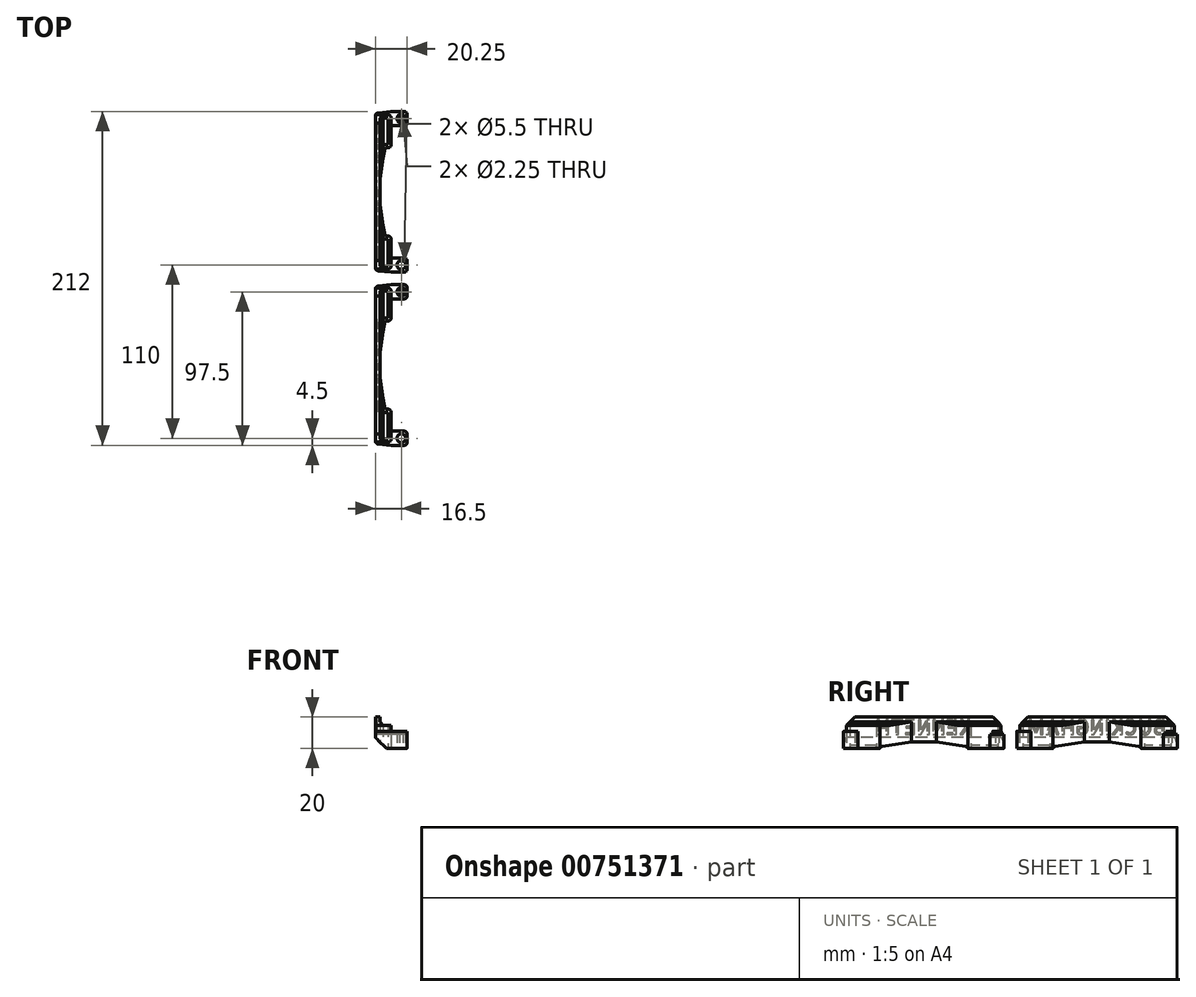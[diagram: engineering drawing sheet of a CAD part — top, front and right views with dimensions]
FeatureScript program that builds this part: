
annotation { "Feature Type Name" : "Feature", "Feature Type Description" : "" }
export const myFeature = defineFeature(function(context is Context, id is Id, definition is map)
    precondition{}
    {
        {
            var Q0;
            Q0=qCreatedBy(makeId("Top.planeOp"),FACE);
            var sketch = newSketch(context, id + "F0", { "sketchPlane" : qUnion([Q0])});
            skLineSegment(sketch, "E0", {"start": v(0, 28) * mm, "end": v(0, -28) * mm, "construction": true});
            skPoint(sketch, "E1", {"position": v(0, 0) * mm});
            skLineSegment(sketch, "E2", {"start": v(0, 28) * mm, "end": v(0, 30) * mm});
            skLineSegment(sketch, "E3", {"start": v(0, 30) * mm, "end": v(0, 47) * mm});
            skLineSegment(sketch, "E4", {"start": v(0, 47) * mm, "end": v(-3, 47) * mm});
            skLineSegment(sketch, "E5", {"start": v(-3, 47) * mm, "end": v(-3, 30) * mm});
            skLineSegment(sketch, "E6", {"start": v(-3, 30) * mm, "end": v(0, 30) * mm});
            skLineSegment(sketch, "E7", {"start": v(-36.95, 0) * mm, "end": v(42, 0) * mm, "construction": true});
            skLineSegment(sketch, "E8", {"start": v(0, 0) * mm, "end": v(8.5, 0) * mm, "construction": true});
            skLineSegment(sketch, "E9", {"start": v(8.5, 46.5) * mm, "end": v(8.5, -46.5) * mm, "construction": true});
            skPoint(sketch, "E10", {"position": v(8.5, 0) * mm});
            skCircle(sketch, "E11", {"center": v(8.5, 46.5) * mm, "radius": 1.13 * mm});
            skCircle(sketch, "E12", {"center": v(8.5, 46.5) * mm, "radius": 2.75 * mm});
            skLineSegment(sketch, "E13.0", {"start": v(2, 28) * mm, "end": v(2, 49) * mm});
            skLineSegment(sketch, "E13.1", {"start": v(-5, 28) * mm, "end": v(2, 28) * mm});
            skLineSegment(sketch, "E13.2", {"start": v(-5, 49) * mm, "end": v(-5, 28) * mm});
            skLineSegment(sketch, "E13.3", {"start": v(2, 49) * mm, "end": v(-5, 49) * mm});
            skLineSegment(sketch, "E14", {"start": v(-5, 49) * mm, "end": v(-8, 49) * mm});
            skLineSegment(sketch, "E15", {"start": v(-8, 49) * mm, "end": v(-8, 50) * mm});
            skLineSegment(sketch, "E16.MirrorCS", {"start": v(-5, -28) * mm, "end": v(2, -28) * mm});
            skLineSegment(sketch, "E17.MirrorCS", {"start": v(2, -28) * mm, "end": v(2, -49) * mm});
            skLineSegment(sketch, "E18.MirrorCS", {"start": v(-5, -49) * mm, "end": v(-5, -28) * mm});
            skLineSegment(sketch, "E19.MirrorCS", {"start": v(2, -49) * mm, "end": v(-5, -49) * mm});
            skLineSegment(sketch, "E20.MirrorCS", {"start": v(0, -30) * mm, "end": v(0, -47) * mm});
            skLineSegment(sketch, "E21.MirrorCS", {"start": v(0, -47) * mm, "end": v(-3, -47) * mm});
            skLineSegment(sketch, "E22.MirrorCS", {"start": v(-3, -47) * mm, "end": v(-3, -30) * mm});
            skLineSegment(sketch, "E23.MirrorCS", {"start": v(-3, -30) * mm, "end": v(0, -30) * mm});
            skLineSegment(sketch, "E24.MirrorCS", {"start": v(-5, -49) * mm, "end": v(-8, -49) * mm});
            skLineSegment(sketch, "E25.MirrorCS", {"start": v(-8, -49) * mm, "end": v(-8, -50) * mm});
            skCircle(sketch, "E26.MirrorC", {"center": v(8.5, -46.5) * mm, "radius": 2.75 * mm});
            skCircle(sketch, "E27.MirrorC", {"center": v(8.5, -46.5) * mm, "radius": 1.13 * mm});
            skLineSegment(sketch, "E28", {"start": v(-8, 49) * mm, "end": v(-8, -49) * mm});
            skLineSegment(sketch, "E29", {"start": v(-5, -28) * mm, "end": v(-5, 28) * mm});
            skLineSegment(sketch, "E30", {"start": v(8.5, 46.5) * mm, "end": v(12.25, 46.5) * mm, "construction": true});
            skLineSegment(sketch, "E31", {"start": v(12.25, 51) * mm, "end": v(12.25, 42) * mm});
            skPoint(sketch, "E32.positionSnap0", {"position": v(12.25, 46.5) * mm});
            skLineSegment(sketch, "E33", {"start": v(12.25, 51) * mm, "end": v(2, 51) * mm});
            skLineSegment(sketch, "E34", {"start": v(2, 51) * mm, "end": v(-8, 50) * mm});
            skLineSegment(sketch, "E35", {"start": v(12.25, 42) * mm, "end": v(2, 42) * mm});
            skLineSegment(sketch, "E36.MirrorCS", {"start": v(12.25, -42) * mm, "end": v(2, -42) * mm});
            skLineSegment(sketch, "E37.MirrorCS", {"start": v(12.25, -51) * mm, "end": v(12.25, -42) * mm});
            skLineSegment(sketch, "E38.MirrorCS", {"start": v(12.25, -51) * mm, "end": v(2, -51) * mm});
            skLineSegment(sketch, "E39.MirrorCS", {"start": v(2, -51) * mm, "end": v(-8, -50) * mm});
            skSolve(sketch);
        }
        {
            var Q0;
            Q0=makeQuery(id+"F0.imprint","IMPRINT",FACE,{"disambiguationData":[TD([[makeQuery(id+"F0.imprint","IMPRINT",EDGE,{"derivedFrom":sQuery(id+"F0.wireOp",EDGE,"E3")}),-1.0]])]});
            var Q1;
            {var subQ3=sQuery(id+"F0.wireOp",EDGE,"E16.MirrorCS");Q1=makeQuery(id+"F0.imprint","IMPRINT",FACE,{"disambiguationData":[TD([[makeQuery(id+"F0.imprint","IMPRINT",EDGE,{"derivedFrom":subQ3}),-1.0]])]});}
            var Q2;
            Q2=makeQuery(id+"F0.imprint","IMPRINT",FACE,{"disambiguationData":[TD([[makeQuery(id+"F0.imprint","IMPRINT",EDGE,{"derivedFrom":sQuery(id+"F0.wireOp",EDGE,"E13.2")}),-1.0]])]});
            extrude(context, id + "F1", {"entities" : qUnion([Q0, Q1, Q2]), "depth" : 14.75 * mm, "offsetDistance" : 25 * mm});
        }
        {
            var Q0;
            {var subQ0=sQuery(id+"F0.wireOp",EDGE,"E19.MirrorCS");Q0=makeQuery(id+"F0.imprint","IMPRINT",FACE,{"disambiguationData":[TD([[makeQuery(id+"F0.imprint","IMPRINT",EDGE,{"derivedFrom":subQ0}),1.0]])]});}
            var Q1;
            Q1=makeQuery(id+"F0.imprint","IMPRINT",FACE,{"disambiguationData":[TD([[makeQuery(id+"F0.imprint","IMPRINT",EDGE,{"derivedFrom":sQuery(id+"F0.wireOp",EDGE,"E12")}),-1.0]])]});
            extrude(context, id + "F2", {"entities" : qUnion([Q0, Q1]), "operationType" : NewBodyOperationType.ADD, "depth" : 9 * mm, "offsetDistance" : 25 * mm});
        }
        {
            var Q0;
            Q0=makeQuery(id+"F0.imprint","IMPRINT",FACE,{"disambiguationData":[TD([[makeQuery(id+"F0.imprint","IMPRINT",EDGE,{"derivedFrom":sQuery(id+"F0.wireOp",EDGE,"E26.MirrorC")}),-1.0]])]});
            var Q1;
            Q1=makeQuery(id+"F0.imprint","IMPRINT",FACE,{"disambiguationData":[TD([[makeQuery(id+"F0.imprint","IMPRINT",EDGE,{"derivedFrom":sQuery(id+"F0.wireOp",EDGE,"E11")}),-1.0]])]});
            extrude(context, id + "F3", {"entities" : qUnion([Q0, Q1]), "operationType" : NewBodyOperationType.ADD, "depth" : 10.9 * mm, "offsetDistance" : 25 * mm});
        }
        {
            var Q0;
            Q0=makeQuery(id+"F0.imprint","IMPRINT",FACE,{"disambiguationData":[TD([[makeQuery(id+"F0.imprint","IMPRINT",EDGE,{"derivedFrom":sQuery(id+"F0.wireOp",EDGE,"E13.2")}),-1.0]])]});
            extrude(context, id + "F4", {"entities" : qUnion([Q0]), "operationType" : NewBodyOperationType.ADD, "depth" : 20 * mm, "offsetDistance" : 25 * mm});
        }
        {
            var Q0;
            Q0=makeQuery(id+"F2.boolean.opBoolean","MERGE",EDGE,{"derivedFrom":[makeQuery(id+"F1.opExtrude","CAP_EDGE",EDGE,{"disambiguationData":[OSD([sQuery(id+"F0.wireOp",EDGE,"E28")])],"isStart":true}),makeQuery(id+"F2.opExtrude","CAP_EDGE",EDGE,{"disambiguationData":[OSD([sQuery(id+"F0.wireOp",EDGE,"E15")])],"isStart":true}),makeQuery(id+"F2.opExtrude","CAP_EDGE",EDGE,{"disambiguationData":[OSD([sQuery(id+"F0.wireOp",EDGE,"E25.MirrorCS")])],"isStart":true})]});
            chamfer(context, id + "F5", {"entities" : qUnion([Q0]), "chamferType" : ChamferType.TWO_OFFSETS, "width1" : 7 * mm, "oppositeDirection" : false, "width2" : 7 * mm, "tangentPropagation" : true});
        }
        {
            var Q0;
            Q0=makeQuery(id+"F1.opExtrude","SWEPT_EDGE",EDGE,{"disambiguationData":[OSD([sQuery(id+"F0.wireOp",EDGE,"E13.1"),sQuery(id+"F0.wireOp",EDGE,"E13.2"),sQuery(id+"F0.wireOp",EDGE,"E29")])]});
            var Q1;
            Q1=makeQuery(id+"F1.opExtrude","SWEPT_EDGE",EDGE,{"disambiguationData":[OSD([sQuery(id+"F0.wireOp",EDGE,"E16.MirrorCS"),sQuery(id+"F0.wireOp",EDGE,"E18.MirrorCS"),sQuery(id+"F0.wireOp",EDGE,"E29")])]});
            chamfer(context, id + "F6", {"entities" : qUnion([Q0, Q1]), "chamferType" : ChamferType.TWO_OFFSETS, "width1" : 3 * mm, "oppositeDirection" : false, "width2" : 20 * mm, "tangentPropagation" : true});
        }
        {
            var Q0;
            Q0=makeQuery(id+"F1.opExtrude","SWEPT_EDGE",EDGE,{"disambiguationData":[OSD([sQuery(id+"F0.wireOp",EDGE,"E13.0"),sQuery(id+"F0.wireOp",EDGE,"E13.1")])]});
            var Q1;
            Q1=makeQuery(id+"F1.opExtrude","SWEPT_EDGE",EDGE,{"disambiguationData":[OSD([sQuery(id+"F0.wireOp",EDGE,"E16.MirrorCS"),sQuery(id+"F0.wireOp",EDGE,"E17.MirrorCS")])]});
            var Q2;
            {var subQ0=sQuery(id+"F0.wireOp",EDGE,"E13.1");Q2=makeQuery(id+"F6.opChamfer","BLEND_EDGE",EDGE,{"blendedFrom":[makeQuery(id+"F1.opExtrude","SWEPT_EDGE",EDGE,{"disambiguationData":[OSD([subQ0,sQuery(id+"F0.wireOp",EDGE,"E13.2"),sQuery(id+"F0.wireOp",EDGE,"E29")])]}),makeQuery(id+"F1.opExtrude","SWEPT_FACE",FACE,{"disambiguationData":[OSD([subQ0])]})],"blendedInto":[makeQuery(id+"F1.opExtrude","SWEPT_FACE",FACE,{"disambiguationData":[OSD([subQ0])]})]});}
            var Q3;
            {var subQ0=sQuery(id+"F0.wireOp",EDGE,"E16.MirrorCS");Q3=makeQuery(id+"F6.opChamfer","BLEND_EDGE",EDGE,{"blendedFrom":[makeQuery(id+"F1.opExtrude","SWEPT_EDGE",EDGE,{"disambiguationData":[OSD([subQ0,sQuery(id+"F0.wireOp",EDGE,"E18.MirrorCS"),sQuery(id+"F0.wireOp",EDGE,"E29")])]}),makeQuery(id+"F1.opExtrude","SWEPT_FACE",FACE,{"disambiguationData":[OSD([subQ0])]})],"blendedInto":[makeQuery(id+"F1.opExtrude","SWEPT_FACE",FACE,{"disambiguationData":[OSD([subQ0])]})]});}
            var Q4;
            Q4=makeQuery(id+"F2.opExtrude","SWEPT_EDGE",EDGE,{"disambiguationData":[OSD([sQuery(id+"F0.wireOp",EDGE,"E25.MirrorCS"),sQuery(id+"F0.wireOp",EDGE,"E39.MirrorCS")])]});
            var Q5;
            Q5=makeQuery(id+"F2.opExtrude","SWEPT_EDGE",EDGE,{"disambiguationData":[OSD([sQuery(id+"F0.wireOp",EDGE,"E38.MirrorCS"),sQuery(id+"F0.wireOp",EDGE,"E39.MirrorCS")])]});
            var Q6;
            Q6=makeQuery(id+"F2.opExtrude","SWEPT_EDGE",EDGE,{"disambiguationData":[OSD([sQuery(id+"F0.wireOp",EDGE,"E15"),sQuery(id+"F0.wireOp",EDGE,"E34")])]});
            var Q7;
            Q7=makeQuery(id+"F2.opExtrude","SWEPT_EDGE",EDGE,{"disambiguationData":[OSD([sQuery(id+"F0.wireOp",EDGE,"E33"),sQuery(id+"F0.wireOp",EDGE,"E34")])]});
            var Q8;
            Q8=makeQuery(id+"F1.opExtrude","SWEPT_EDGE",EDGE,{"disambiguationData":[OSD([sQuery(id+"F0.wireOp",EDGE,"E13.0"),sQuery(id+"F0.wireOp",EDGE,"E13.3")])]});
            var Q9;
            Q9=makeQuery(id+"F1.opExtrude","SWEPT_EDGE",EDGE,{"disambiguationData":[OSD([sQuery(id+"F0.wireOp",EDGE,"E17.MirrorCS"),sQuery(id+"F0.wireOp",EDGE,"E19.MirrorCS")])]});
            var Q10;
            Q10=makeQuery(id+"F2.opExtrude","SWEPT_EDGE",EDGE,{"disambiguationData":[OSD([sQuery(id+"F0.wireOp",EDGE,"E36.MirrorCS"),sQuery(id+"F0.wireOp",EDGE,"E37.MirrorCS")])]});
            var Q11;
            Q11=makeQuery(id+"F2.opExtrude","SWEPT_EDGE",EDGE,{"disambiguationData":[OSD([sQuery(id+"F0.wireOp",EDGE,"E37.MirrorCS"),sQuery(id+"F0.wireOp",EDGE,"E38.MirrorCS")])]});
            var Q12;
            Q12=makeQuery(id+"F2.opExtrude","SWEPT_EDGE",EDGE,{"disambiguationData":[OSD([sQuery(id+"F0.wireOp",EDGE,"E31"),sQuery(id+"F0.wireOp",EDGE,"E35")])]});
            var Q13;
            Q13=makeQuery(id+"F2.opExtrude","SWEPT_EDGE",EDGE,{"disambiguationData":[OSD([sQuery(id+"F0.wireOp",EDGE,"E31"),sQuery(id+"F0.wireOp",EDGE,"E33")])]});
            var Q14;
            Q14=makeQuery(id+"F2.opExtrude","SWEPT_EDGE",EDGE,{"disambiguationData":[OSD([sQuery(id+"F0.wireOp",EDGE,"E13.0"),sQuery(id+"F0.wireOp",EDGE,"E35")])]});
            var Q15;
            Q15=makeQuery(id+"F2.opExtrude","SWEPT_EDGE",EDGE,{"disambiguationData":[OSD([sQuery(id+"F0.wireOp",EDGE,"E17.MirrorCS"),sQuery(id+"F0.wireOp",EDGE,"E36.MirrorCS")])]});
            fillet(context, id + "F7", {"entities" : qUnion([Q0, Q1, Q2, Q3, Q4, Q5, Q6, Q7, Q8, Q9, Q10, Q11, Q12, Q13, Q14, Q15]), "radius" : 2 * mm, "tangentPropagation" : true, "allowEdgeOverflow" : false});
        }
        {
            var Q0;
            {var subQ0=sQuery(id+"F0.wireOp",EDGE,"E29");Q0=makeQuery(id+"F4.boolean.opBoolean","INTERSECT",EDGE,{"disambiguationData":[OD(1.0)],"derivedFrom":[makeQuery(id+"F1.opExtrude","CAP_FACE",FACE,{"disambiguationData":[OSD([sQuery(id+"F0.wireOp",EDGE,"E3"),sQuery(id+"F0.wireOp",EDGE,"E4"),sQuery(id+"F0.wireOp",EDGE,"E5"),sQuery(id+"F0.wireOp",EDGE,"E6"),sQuery(id+"F0.wireOp",EDGE,"E13.0"),sQuery(id+"F0.wireOp",EDGE,"E13.1"),sQuery(id+"F0.wireOp",EDGE,"E13.3"),sQuery(id+"F0.wireOp",EDGE,"E14"),sQuery(id+"F0.wireOp",EDGE,"E16.MirrorCS"),sQuery(id+"F0.wireOp",EDGE,"E17.MirrorCS"),sQuery(id+"F0.wireOp",EDGE,"E19.MirrorCS"),sQuery(id+"F0.wireOp",EDGE,"E20.MirrorCS"),sQuery(id+"F0.wireOp",EDGE,"E21.MirrorCS"),sQuery(id+"F0.wireOp",EDGE,"E22.MirrorCS"),sQuery(id+"F0.wireOp",EDGE,"E23.MirrorCS"),sQuery(id+"F0.wireOp",EDGE,"E24.MirrorCS"),sQuery(id+"F0.wireOp",EDGE,"E28"),subQ0])],"isStart":false}),makeQuery(id+"F4.opExtrude","SWEPT_FACE",FACE,{"disambiguationData":[OSD([sQuery(id+"F0.wireOp",EDGE,"E13.2"),sQuery(id+"F0.wireOp",EDGE,"E18.MirrorCS"),subQ0])]})]});}
            var Q1;
            {var subQ0=sQuery(id+"F0.wireOp",EDGE,"E29");Q1=makeQuery(id+"F4.boolean.opBoolean","INTERSECT",EDGE,{"disambiguationData":[OD(0.0)],"derivedFrom":[makeQuery(id+"F1.opExtrude","CAP_FACE",FACE,{"disambiguationData":[OSD([sQuery(id+"F0.wireOp",EDGE,"E3"),sQuery(id+"F0.wireOp",EDGE,"E4"),sQuery(id+"F0.wireOp",EDGE,"E5"),sQuery(id+"F0.wireOp",EDGE,"E6"),sQuery(id+"F0.wireOp",EDGE,"E13.0"),sQuery(id+"F0.wireOp",EDGE,"E13.1"),sQuery(id+"F0.wireOp",EDGE,"E13.3"),sQuery(id+"F0.wireOp",EDGE,"E14"),sQuery(id+"F0.wireOp",EDGE,"E16.MirrorCS"),sQuery(id+"F0.wireOp",EDGE,"E17.MirrorCS"),sQuery(id+"F0.wireOp",EDGE,"E19.MirrorCS"),sQuery(id+"F0.wireOp",EDGE,"E20.MirrorCS"),sQuery(id+"F0.wireOp",EDGE,"E21.MirrorCS"),sQuery(id+"F0.wireOp",EDGE,"E22.MirrorCS"),sQuery(id+"F0.wireOp",EDGE,"E23.MirrorCS"),sQuery(id+"F0.wireOp",EDGE,"E24.MirrorCS"),sQuery(id+"F0.wireOp",EDGE,"E28"),subQ0])],"isStart":false}),makeQuery(id+"F4.opExtrude","SWEPT_FACE",FACE,{"disambiguationData":[OSD([sQuery(id+"F0.wireOp",EDGE,"E13.2"),sQuery(id+"F0.wireOp",EDGE,"E18.MirrorCS"),subQ0])]})]});}
            chamfer(context, id + "F8", {"entities" : qUnion([Q0, Q1]), "width" : 2 * mm, "tangentPropagation" : true});
        }
        {
            var Q0;
            Q0=makeQuery(id+"F4.opExtrude","CAP_EDGE",EDGE,{"disambiguationData":[OSD([sQuery(id+"F0.wireOp",EDGE,"E24.MirrorCS")])],"isStart":false});
            var Q1;
            Q1=makeQuery(id+"F4.opExtrude","CAP_EDGE",EDGE,{"disambiguationData":[OSD([sQuery(id+"F0.wireOp",EDGE,"E14")])],"isStart":false});
            chamfer(context, id + "F9", {"entities" : qUnion([Q0, Q1]), "width" : 5.25 * mm, "tangentPropagation" : true});
        }
        {
            var Q0;
            Q0=makeQuery(id+"F1.opExtrude","SWEPT_BODY",BODY,{"disambiguationData":[OSD([sQuery(id+"F0.wireOp",EDGE,"E3"),sQuery(id+"F0.wireOp",EDGE,"E4"),sQuery(id+"F0.wireOp",EDGE,"E5"),sQuery(id+"F0.wireOp",EDGE,"E6"),sQuery(id+"F0.wireOp",EDGE,"E13.0"),sQuery(id+"F0.wireOp",EDGE,"E13.1"),sQuery(id+"F0.wireOp",EDGE,"E13.3"),sQuery(id+"F0.wireOp",EDGE,"E14"),sQuery(id+"F0.wireOp",EDGE,"E16.MirrorCS"),sQuery(id+"F0.wireOp",EDGE,"E17.MirrorCS"),sQuery(id+"F0.wireOp",EDGE,"E19.MirrorCS"),sQuery(id+"F0.wireOp",EDGE,"E20.MirrorCS"),sQuery(id+"F0.wireOp",EDGE,"E21.MirrorCS"),sQuery(id+"F0.wireOp",EDGE,"E22.MirrorCS"),sQuery(id+"F0.wireOp",EDGE,"E23.MirrorCS"),sQuery(id+"F0.wireOp",EDGE,"E24.MirrorCS"),sQuery(id+"F0.wireOp",EDGE,"E28"),sQuery(id+"F0.wireOp",EDGE,"E29")])]});
            transform(context, id + "F10", {"entities" : qUnion([Q0]), "transformType" : TransformType.TRANSLATION_3D, "dx" : 0 * mm, "dy" : 110 * mm, "dz" : 0 * mm, "makeCopy" : true});
        }
        {
            var Q0;
            {var subQ0=sQuery(id+"F0.wireOp",EDGE,"E28");Q0=makeQuery(id+"F4.boolean.opBoolean","MERGE",FACE,{"derivedFrom":[makeQuery(id+"F2.boolean.opBoolean","MERGE",FACE,{"derivedFrom":[makeQuery(id+"F1.opExtrude","SWEPT_FACE",FACE,{"disambiguationData":[OSD([subQ0])]}),makeQuery(id+"F2.opExtrude","SWEPT_FACE",FACE,{"disambiguationData":[OSD([sQuery(id+"F0.wireOp",EDGE,"E15")])]}),makeQuery(id+"F2.opExtrude","SWEPT_FACE",FACE,{"disambiguationData":[OSD([sQuery(id+"F0.wireOp",EDGE,"E25.MirrorCS")])]})]}),makeQuery(id+"F4.opExtrude","SWEPT_FACE",FACE,{"disambiguationData":[OSD([subQ0])]})]});}
            var sketch = newSketch(context, id + "F11", { "sketchPlane" : qUnion([Q0])});
            skLineSegment(sketch, "E40", {"start": v(0, 7) * mm, "end": v(0, 20) * mm, "construction": true});
            skPoint(sketch, "E41", {"position": v(0, 13.5) * mm});
            skText(sketch, "E42", { "text": "KENNETH", "fontName": "AllertaStencil-Regular.ttf"});
            skLineSegment(sketch, "E43", {"start": v(-30.55, 14) * mm, "end": v(-30.55, 13) * mm});
            skPoint(sketch, "E44", {"position": v(-30.55, 13.5) * mm});
            skLineSegment(sketch, "E45", {"start": v(-30.55, 14) * mm, "end": v(30.55, 14) * mm, "construction": true});
            skLineSegment(sketch, "E46", {"start": v(-30.55, 13) * mm, "end": v(30.55, 13) * mm, "construction": true});
            skLineSegment(sketch, "E47", {"start": v(30.55, 13) * mm, "end": v(30.55, 14) * mm});
            const initialGuessF11  = {"E42": [-0.03055, 0.00875, 1, 0, 0.0095]};
            skSetInitialGuess(sketch, initialGuessF11);
            skSolve(sketch);
        }
        {
            var Q0;
            {var subQ0=sQuery(id+"F0.wireOp",EDGE,"E28");Q0=makeQuery(id+"F10.opPattern","COPY",FACE,{"derivedFrom":makeQuery(id+"F4.boolean.opBoolean","MERGE",FACE,{"derivedFrom":[makeQuery(id+"F2.boolean.opBoolean","MERGE",FACE,{"derivedFrom":[makeQuery(id+"F1.opExtrude","SWEPT_FACE",FACE,{"disambiguationData":[OSD([subQ0])]}),makeQuery(id+"F2.opExtrude","SWEPT_FACE",FACE,{"disambiguationData":[OSD([sQuery(id+"F0.wireOp",EDGE,"E15")])]}),makeQuery(id+"F2.opExtrude","SWEPT_FACE",FACE,{"disambiguationData":[OSD([sQuery(id+"F0.wireOp",EDGE,"E25.MirrorCS")])]})]}),makeQuery(id+"F4.opExtrude","SWEPT_FACE",FACE,{"disambiguationData":[OSD([subQ0])]})]}),"instanceName":"1"});}
            var sketch = newSketch(context, id + "F12", { "sketchPlane" : qUnion([Q0])});
            skLineSegment(sketch, "E48", {"start": v(-110, 7) * mm, "end": v(-110, 20) * mm, "construction": true});
            skPoint(sketch, "E49", {"position": v(-110, 13.5) * mm});
            skText(sketch, "E50", { "text": "BUCKINGHAM", "fontName": "AllertaStencil-Regular.ttf"});
            const initialGuessF12  = {"E50": [-0.154, 0.00875, 1, 0, 0.0095]};
            skSetInitialGuess(sketch, initialGuessF12);
            skSolve(sketch);
        }
        {
            var Q0;
            Q0 = qSketchRegion(id + "F11", true);
            var Q1;
            Q1 = qSketchRegion(id + "F12", true);
            extrude(context, id + "F13", {"entities" : qUnion([Q0, Q1]), "operationType" : NewBodyOperationType.REMOVE, "oppositeDirection" : true, "depth" : 1 * mm, "offsetDistance" : 25 * mm});
        }
        {
            var Q0;
            Q0=makeQuery(id+"F11.imprint","IMPRINT",FACE,{"disambiguationData":[TD([[makeQuery(id+"F11.imprint","IMPRINT",EDGE,{"derivedFrom":sQuery(id+"F11.wireOp",EDGE,"E42.sketch_text.stroke-0")}),-1.0]])]});
            extrude(context, id + "F14", {"entities" : qUnion([Q0]), "oppositeDirection" : true, "depth" : 2 * mm, "offsetDistance" : 25 * mm});
        }
        {
            var Q0;
            Q0=makeQuery(id+"F14.opExtrude","SWEPT_BODY",BODY,{"disambiguationData":[OSD([sQuery(id+"F11.wireOp",EDGE,"E42.sketch_text.stroke-0"),sQuery(id+"F11.wireOp",EDGE,"E42.sketch_text.stroke-1"),sQuery(id+"F11.wireOp",EDGE,"E42.sketch_text.stroke-2"),sQuery(id+"F11.wireOp",EDGE,"E42.sketch_text.stroke-3")])]});
            deleteBodies(context, id + "F15", {"entities" : qUnion([Q0])});
        }
    });
